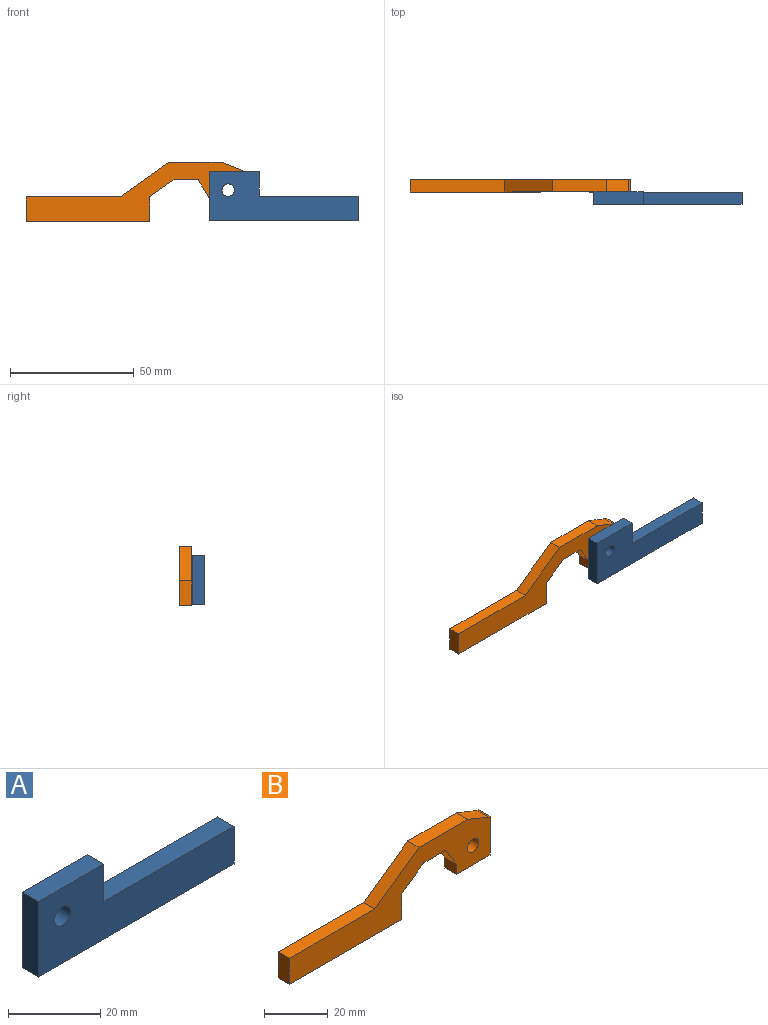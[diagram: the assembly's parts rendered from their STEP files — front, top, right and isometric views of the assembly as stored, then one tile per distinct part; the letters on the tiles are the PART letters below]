
ASSEMBLY  parts=2 mates=1
PART A: 9 faces, bbox 60x5x20 mm
  f0: plane 40x5mm, normal (0,0,1), area 200mm2, adj f1,f5,f7,f8
  f1: plane 10x5mm, normal (1,0,0), area 50mm2, adj f0,f2,f7,f8
  f2: plane 20x5mm, normal (0,0,1), area 100mm2, adj f1,f3,f7,f8
  f3: plane 20x5mm, normal (-1,0,0), area 100mm2, adj f2,f4,f7,f8
  f4: plane 60x5mm, normal (0,0,-1), area 300mm2, adj f3,f5,f7,f8
  f5: plane 10x5mm, normal (1,0,0), area 50mm2, adj f0,f4,f7,f8
  f6: cylinder r=2.5mm len=5mm, axis (0,-1,0), area 78.5mm2, adj f7,f8
  f7: plane 60x20mm, normal (0,1,0), area 780.4mm2, adj f0,f1,f2,f3,f4,f5,f6
  f8: plane 60x20mm, normal (0,-1,0), area 780.4mm2, adj f0,f1,f2,f3,f4,f5,f6
PART B: 17 faces, bbox 89.2x5x23.9 mm
  f0: plane 10x5mm, normal (1,0,0), area 50mm2, adj f1,f13,f15,f16
  f1: plane 9.84x6.89mm, normal (0.57,0,-0.82), area 60mm2, adj f0,f2,f15,f16
  f2: plane 9.71x5mm, normal (0,0,-1), area 48.6mm2, adj f1,f3,f15,f16
  f3: plane 7.67x5mm, normal (-0.85,0,-0.52), area 44.9mm2, adj f2,f4,f15,f16
  f4: plane 5x4.03mm, normal (-1,0,0), area 20.1mm2, adj f3,f5,f15,f16
  f5: plane 15x5mm, normal (0,0,-1), area 75mm2, adj f4,f6,f15,f16
  f6: plane 15x5mm, normal (1,0,0), area 75mm2, adj f5,f7,f15,f16
  f7: plane 5x0.81mm, normal (0,0,1), area 4mm2, adj f6,f8,f15,f16
  f8: plane 9.12x5mm, normal (0.38,0,0.93), area 49.2mm2, adj f7,f9,f15,f16
  f9: plane 21.59x5mm, normal (0,0,1), area 108mm2, adj f8,f10,f15,f16
  f10: plane 19.61x13.88mm, normal (-0.58,0,0.82), area 120.1mm2, adj f9,f11,f15,f16
  f11: plane 38.07x5mm, normal (0,0,1), area 190.4mm2, adj f10,f12,f15,f16
  f12: plane 10x5mm, normal (-1,0,0), area 50mm2, adj f11,f13,f15,f16
  f13: plane 50x5mm, normal (0,0,-1), area 250mm2, adj f0,f12,f15,f16
  f14: cylinder r=2.5mm len=5mm, axis (0,1,0), area 78.5mm2, adj f15,f16
  f15: plane 89.21x23.88mm, normal (0,-1,0), area 991.6mm2, adj f0,f1,f2,f3,f4,f5,f6,f7
  f16: plane 89.21x23.88mm, normal (0,1,0), area 991.6mm2, adj f0,f1,f2,f3,f4,f5,f6,f7
PLACE A t=(-26.53,-15,-0.48)mm fixed
PLACE B rot(axis=(0,-1,0),0.1deg) t=(-26.5,0,-0.65)mm
MATE revolute A.f6 <-> B.f14  axis (0,1,0) through (-39.03,-5,12.02)mm
